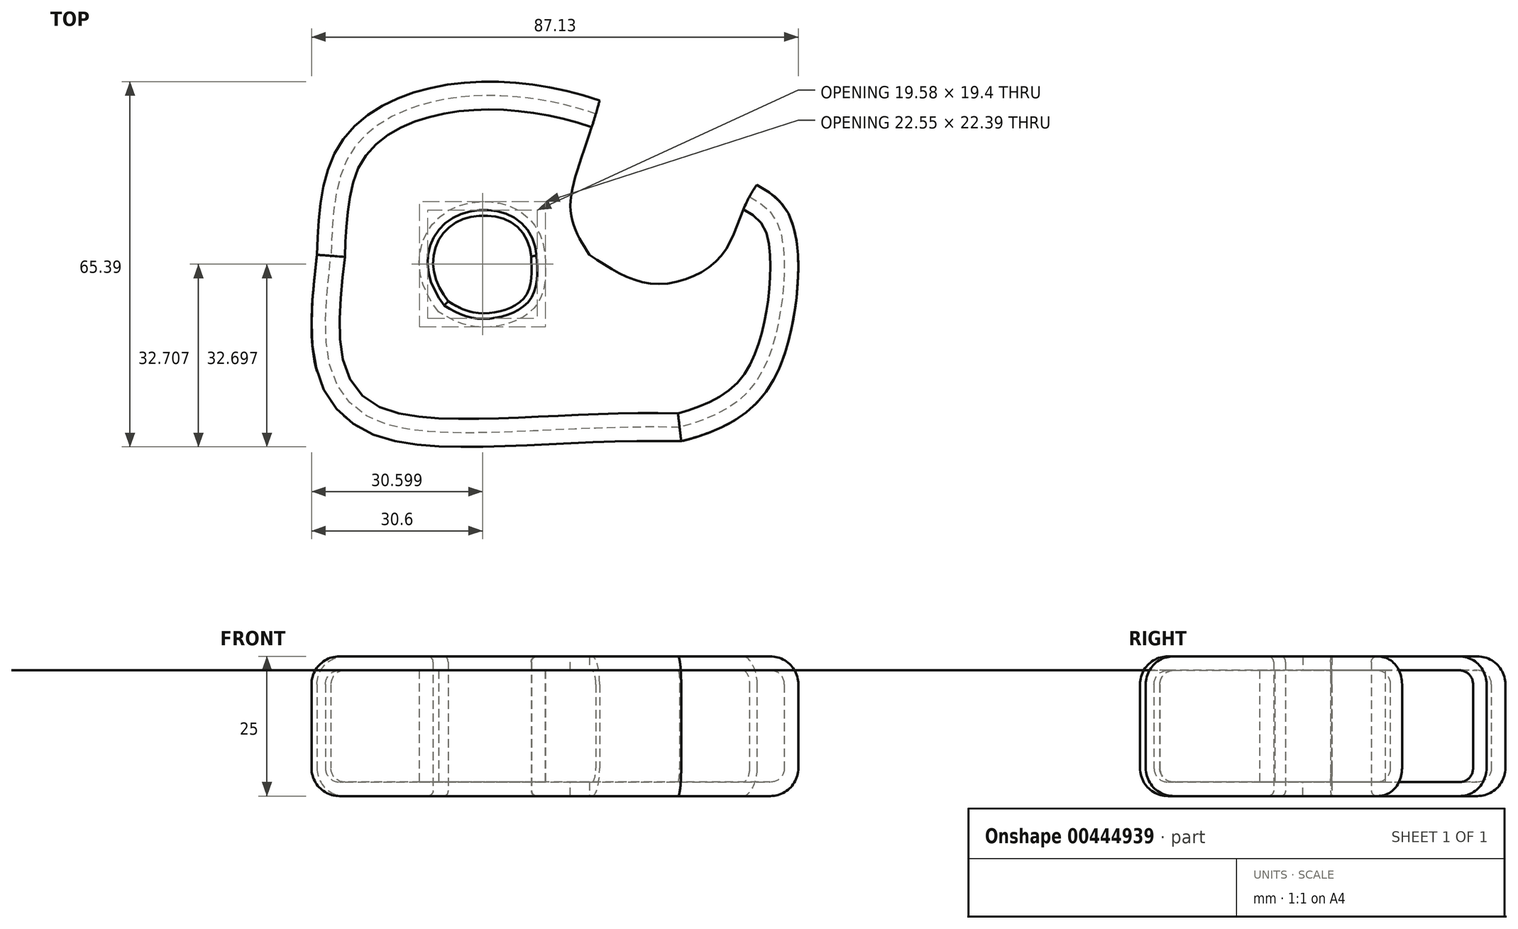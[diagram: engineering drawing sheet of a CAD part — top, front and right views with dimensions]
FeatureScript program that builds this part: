
annotation { "Feature Type Name" : "Feature", "Feature Type Description" : "" }
export const myFeature = defineFeature(function(context is Context, id is Id, definition is map)
    precondition{}
    {
        {
            var Q0;
            Q0=qCreatedBy(makeId("Top.planeOp"),FACE);
            var sketch = newSketch(context, id + "F0", { "sketchPlane" : qUnion([Q0])});
            skFitSpline(sketch, "E0", {"points": [v(-5.38, 43.8) * mm, v(-35.1, 46.15) * mm, v(-52.06, 35.72) * mm, v(-55.97, 16.17) * mm], "startDerivative": vector(-78.32, 26.8) * mm, "endDerivative": vector(-2.86, -68.42) * mm});
            skFitSpline(sketch, "E1", {"points": [v(-55.97, 16.17) * mm, v(-55.97, -4.7) * mm, v(-44.76, -16.43) * mm, v(9.22, -17.21) * mm], "startDerivative": vector(-8.73, -77.94) * mm, "endDerivative": vector(142.6, -3.4) * mm});
            skFitSpline(sketch, "E2", {"points": [v(9.22, -17.21) * mm, v(23.82, -9.13) * mm, v(29.56, 6.26) * mm, v(29.56, 20.34) * mm, v(22.78, 28.68) * mm], "startDerivative": vector(69.7, 17.43) * mm, "endDerivative": vector(-61.52, 32.57) * mm});
            skFitSpline(sketch, "E3", {"points": [v(22.78, 28.68) * mm, v(16.52, 16.17) * mm, v(4.53, 10.95) * mm, v(-7.2, 16.17) * mm], "startDerivative": vector(-27.46, -36.6) * mm, "endDerivative": vector(-34.53, 22.97) * mm});
            skFitSpline(sketch, "E4", {"points": [v(-7.2, 16.17) * mm, v(-10.6, 24.51) * mm, v(-5.38, 43.8) * mm], "startDerivative": vector(-11.89, 18.47) * mm, "endDerivative": vector(10.46, 40.53) * mm});
            skFitSpline(sketch, "E5", {"points": [v(-32.5, 7.82) * mm, v(-27.02, 5.74) * mm, v(-18.94, 8.34) * mm, v(-17.64, 15.9) * mm], "startDerivative": vector(16.16, -9.53) * mm, "endDerivative": vector(-1.37, 25) * mm});
            skFitSpline(sketch, "E6", {"points": [v(-17.64, 15.9) * mm, v(-22.07, 22.43) * mm, v(-31.2, 21.9) * mm, v(-35.1, 15.9) * mm, v(-32.5, 7.82) * mm], "startDerivative": vector(-3.18, 38.19) * mm, "endDerivative": vector(24.53, -33.72) * mm});
            skSolve(sketch);
        }
        {
            var Q0;
            Q0 = qSketchRegion(id + "F0", true);
            extrude(context, id + "F1", {"entities" : qUnion([Q0]), "depth" : 25 * mm});
        }
        {
            var Q0;
            Q0=makeQuery(id+"F1.opExtrude","CAP_EDGE",EDGE,{"disambiguationData":[OSD([sQuery(id+"F0.wireOp",EDGE,"E0")])],"isStart":false});
            var Q1;
            Q1=makeQuery(id+"F1.opExtrude","CAP_EDGE",EDGE,{"disambiguationData":[OSD([sQuery(id+"F0.wireOp",EDGE,"E1")])],"isStart":false});
            var Q2;
            Q2=makeQuery(id+"F1.opExtrude","CAP_EDGE",EDGE,{"disambiguationData":[OSD([sQuery(id+"F0.wireOp",EDGE,"E2")])],"isStart":false});
            var Q3;
            Q3=makeQuery(id+"F1.opExtrude","CAP_EDGE",EDGE,{"disambiguationData":[OSD([sQuery(id+"F0.wireOp",EDGE,"E0")])],"isStart":true});
            var Q4;
            Q4=makeQuery(id+"F1.opExtrude","CAP_EDGE",EDGE,{"disambiguationData":[OSD([sQuery(id+"F0.wireOp",EDGE,"E1")])],"isStart":true});
            var Q5;
            Q5=makeQuery(id+"F1.opExtrude","CAP_EDGE",EDGE,{"disambiguationData":[OSD([sQuery(id+"F0.wireOp",EDGE,"E2")])],"isStart":true});
            fillet(context, id + "F2", {"entities" : qUnion([Q0, Q1, Q2, Q3, Q4, Q5]), "radius" : 5 * mm, "tangentPropagation" : true, "allowEdgeOverflow" : false});
        }
        {
            var Q0;
            Q0=makeQuery(id+"F1.opExtrude","CAP_EDGE",EDGE,{"disambiguationData":[OSD([sQuery(id+"F0.wireOp",EDGE,"E6")])],"isStart":true});
            var Q1;
            Q1=makeQuery(id+"F1.opExtrude","CAP_EDGE",EDGE,{"disambiguationData":[OSD([sQuery(id+"F0.wireOp",EDGE,"E5")])],"isStart":true});
            var Q2;
            Q2=makeQuery(id+"F1.opExtrude","CAP_EDGE",EDGE,{"disambiguationData":[OSD([sQuery(id+"F0.wireOp",EDGE,"E6")])],"isStart":false});
            var Q3;
            Q3=makeQuery(id+"F1.opExtrude","CAP_EDGE",EDGE,{"disambiguationData":[OSD([sQuery(id+"F0.wireOp",EDGE,"E5")])],"isStart":false});
            fillet(context, id + "F3", {"entities" : qUnion([Q0, Q1, Q2, Q3]), "radius" : 1 * mm, "tangentPropagation" : true, "allowEdgeOverflow" : false});
        }
        {
            var Q0;
            Q0=makeQuery(id+"F1.opExtrude","SWEPT_FACE",FACE,{"disambiguationData":[OSD([sQuery(id+"F0.wireOp",EDGE,"E4")])]});
            var Q1;
            Q1=makeQuery(id+"F1.opExtrude","SWEPT_FACE",FACE,{"disambiguationData":[OSD([sQuery(id+"F0.wireOp",EDGE,"E3")])]});
            shell(context, id + "F4", {"entities" : qUnion([Q0, Q1]), "thickness" : 2.5 * mm});
        }
    });
